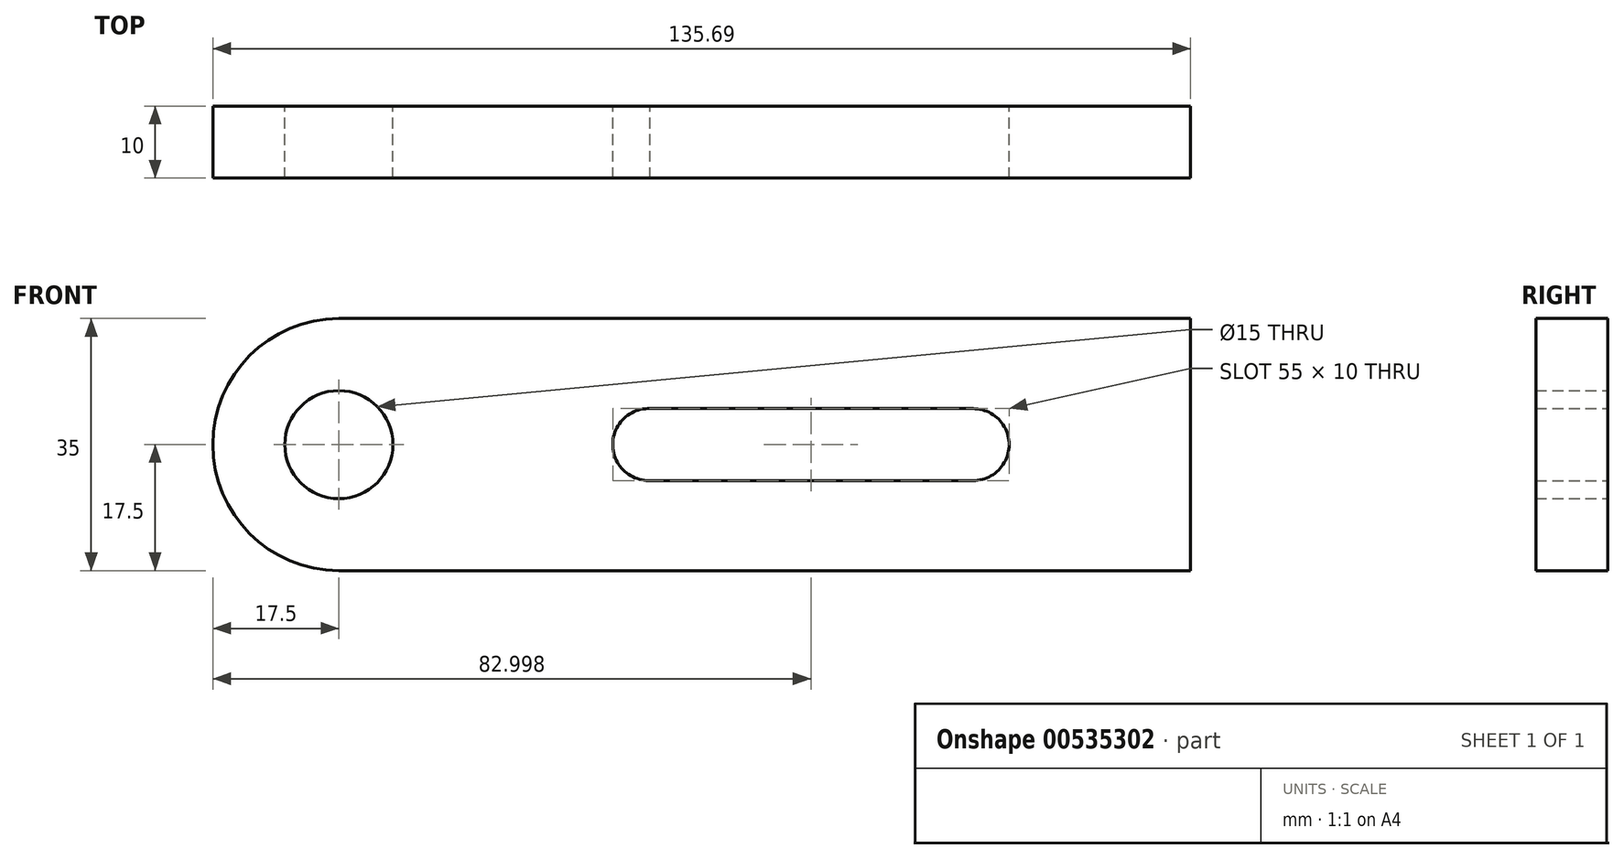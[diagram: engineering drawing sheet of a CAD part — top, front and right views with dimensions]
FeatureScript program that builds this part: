
annotation { "Feature Type Name" : "Feature", "Feature Type Description" : "" }
export const myFeature = defineFeature(function(context is Context, id is Id, definition is map)
    precondition{}
    {
        {
            var Q0;
            Q0=qCreatedBy(makeId("Front.planeOp"),FACE);
            var sketch = newSketch(context, id + "F0", { "sketchPlane" : qUnion([Q0])});
            skCircle(sketch, "E0", {"center": v(0, 0) * mm, "radius": 7.5 * mm});
            skArc(sketch, "E1", {"start": v(0, 17.5) * mm, "mid": v(-17.5, 0) * mm, "end": v(0, -17.5) * mm});
            skLineSegment(sketch, "E2", {"start": v(0, 17.5) * mm, "end": v(118.19, 17.5) * mm});
            skLineSegment(sketch, "E3", {"start": v(118.19, 17.5) * mm, "end": v(118.19, -17.5) * mm});
            skLineSegment(sketch, "E4", {"start": v(118.19, -17.5) * mm, "end": v(0, -17.5) * mm});
            skArc(sketch, "E5", {"start": v(43.18, 5) * mm, "mid": v(38, 0.1) * mm, "end": v(43, -5) * mm});
            skArc(sketch, "E6", {"start": v(88, -5) * mm, "mid": v(93, 0) * mm, "end": v(88, 5) * mm});
            skLineSegment(sketch, "E7", {"start": v(42.8, 5) * mm, "end": v(88, 5) * mm});
            skLineSegment(sketch, "E8", {"start": v(43, -5) * mm, "end": v(88, -5) * mm});
            skSolve(sketch);
        }
        {
            var Q0;
            Q0 = qSketchRegion(id + "F0", true);
            extrude(context, id + "F1", {"entities" : qUnion([Q0]), "depth" : 10 * mm, "offsetDistance" : 25 * mm});
        }
    });
